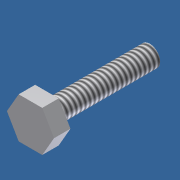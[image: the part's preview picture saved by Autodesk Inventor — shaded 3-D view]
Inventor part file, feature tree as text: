
AUTODESK INVENTOR PART (.ipt)
format: ipt  version: 2012 (Build 160160000, 160)  size: 80,384 bytes
history: native  units: in
note: dims shown in document units (in); Inventor stores cm internally (conversion verified against a paired STEP export)
features: extrude x2, sketch x1, thread x1
ambient origin geometry x8: Origin, YZ Plane, XZ Plane, XY Plane, X Axis, Y Axis, Z Axis, Center Point
bodies: Solid1 (feature_tree)
feature tree (4):
  sketch  "Sketch1"  dims[d10=0.495in d11=1.25in d12=0.0in d13=0.2in d14=0.0in d15=0.0in d16=0.0in]
  extrude  "Extrusion1"  Depth=1.25in TaperAngle=0.0deg
  extrude  "Extrusion2"  Depth=0.2in TaperAngle=0.0deg
  thread  "Thread1"  [1 undecoded]
note: 1 required parameter value undecoded (feature->parameter linkage not recoverable at this tier; creation-order binding heuristic only, values carry confidence <= 0.55)
